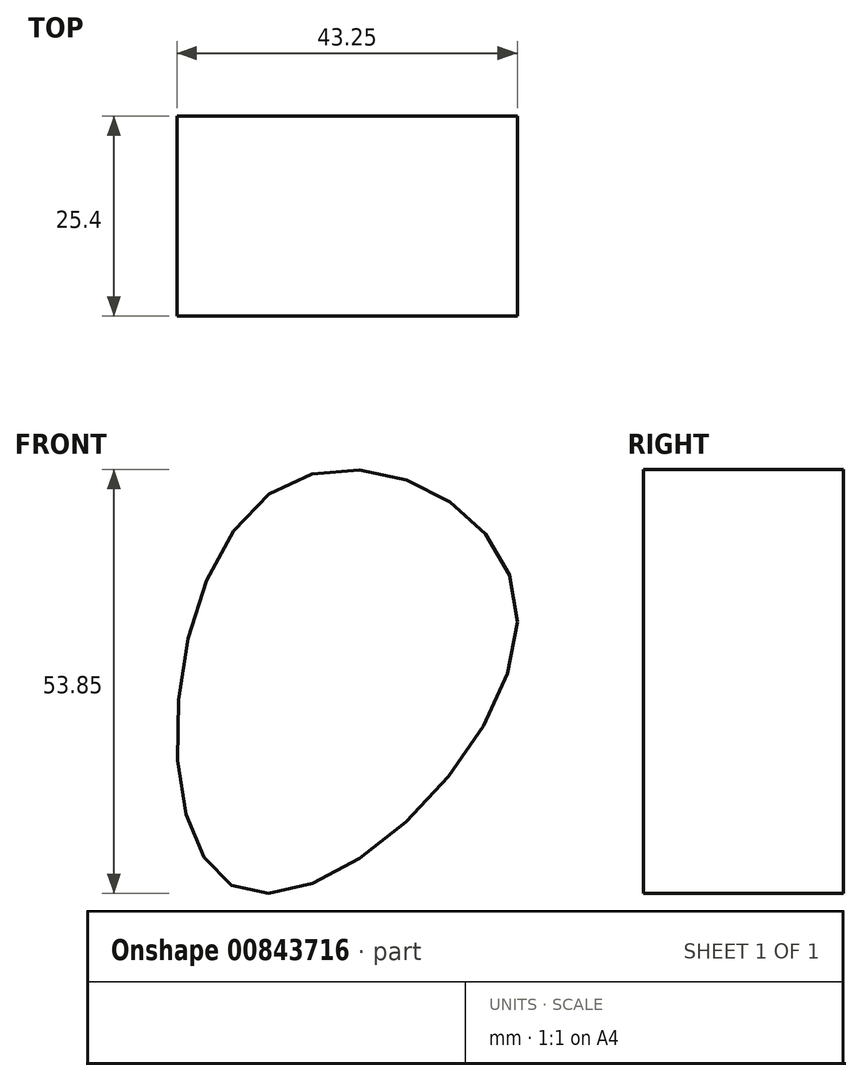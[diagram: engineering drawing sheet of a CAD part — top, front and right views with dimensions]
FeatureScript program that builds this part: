
annotation { "Feature Type Name" : "Feature", "Feature Type Description" : "" }
export const myFeature = defineFeature(function(context is Context, id is Id, definition is map)
    precondition{}
    {
        {
            var Q0;
            Q0=qCreatedBy(makeId("Front.planeOp"),FACE);
            var sketch = newSketch(context, id + "F0", { "sketchPlane" : qUnion([Q0])});
            skFitSpline(sketch, "E0", {"points": [v(-81, 47.52) * mm, v(-49.5, 32.77) * mm, v(-85.26, -2.41) * mm, v(-81, 47.52) * mm]});
            skSolve(sketch);
        }
        {
            var Q0;
            Q0=makeQuery(id+"F0.imprint","IMPRINT",FACE,{"disambiguationData":[TD([[makeQuery(id+"F0.imprint","IMPRINT",EDGE,{"derivedFrom":sQuery(id+"F0.wireOp",EDGE,"E0")}),-1.0]])]});
            extrude(context, id + "F1", {"entities" : qUnion([Q0]), "depth" : 25.4 * mm, "offsetDistance" : 25.4 * mm});
        }
    });
